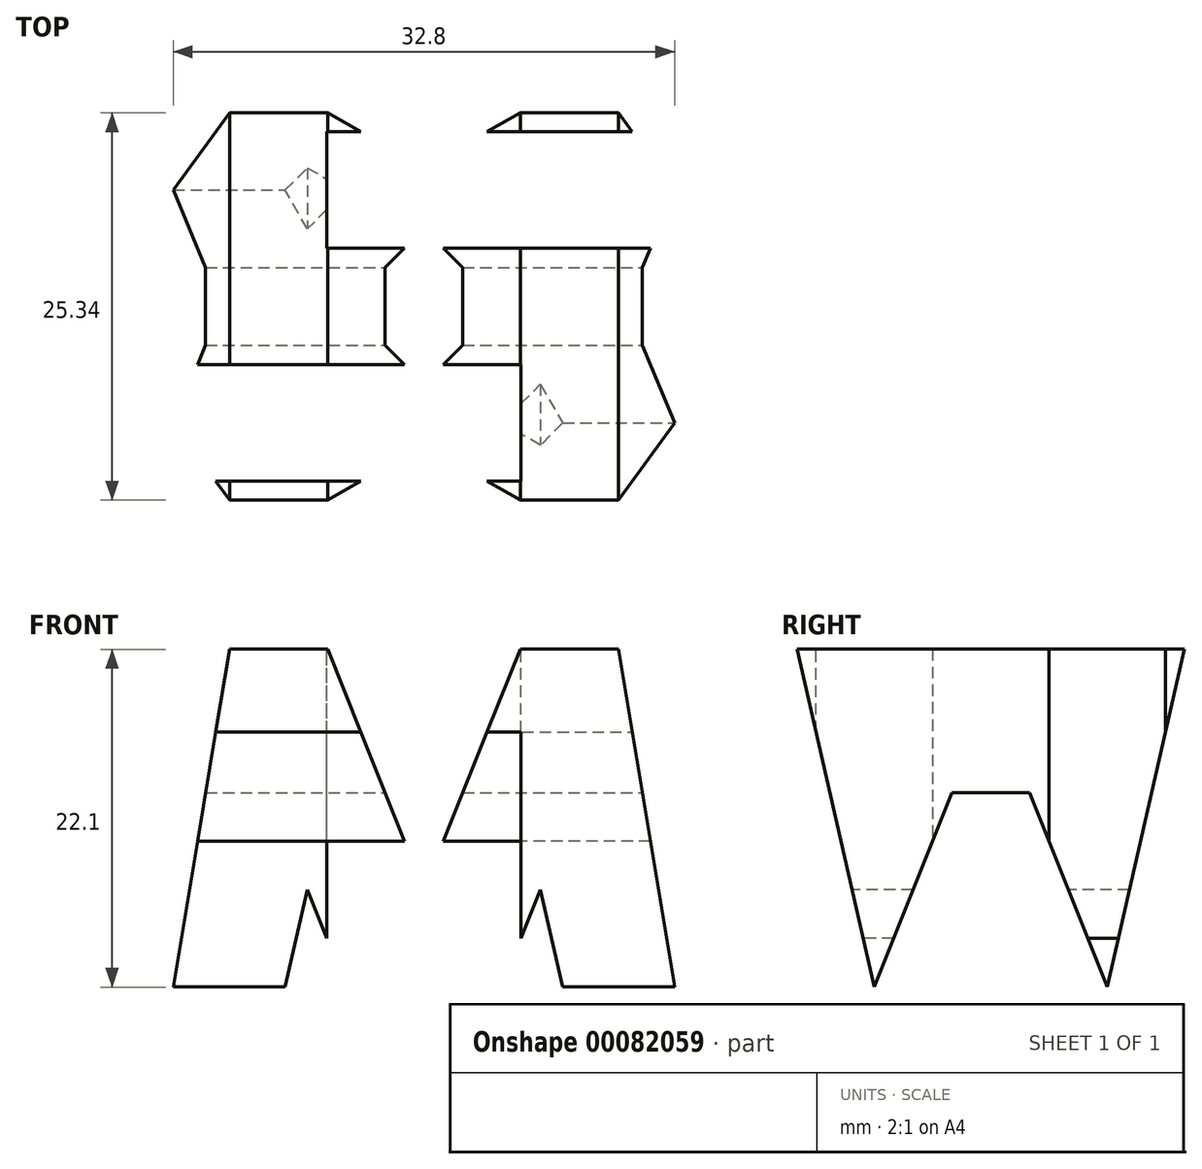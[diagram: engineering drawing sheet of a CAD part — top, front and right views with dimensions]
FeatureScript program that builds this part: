
annotation { "Feature Type Name" : "Feature", "Feature Type Description" : "" }
export const myFeature = defineFeature(function(context is Context, id is Id, definition is map)
    precondition{}
    {
        {
            var Q0;
            Q0=qCreatedBy(makeId("Front.planeOp"),FACE);
            var sketch = newSketch(context, id + "F0", { "sketchPlane" : qUnion([Q0])});
            skLineSegment(sketch, "E0", {"start": v(0, 0) * mm, "end": v(0, 37.97) * mm});
            skLineSegment(sketch, "E1", {"start": v(0, 37.97) * mm, "end": v(38.1, 37.97) * mm});
            skLineSegment(sketch, "E2", {"start": v(38.1, 37.97) * mm, "end": v(38.1, 0) * mm});
            skLineSegment(sketch, "E3", {"start": v(38.1, 0) * mm, "end": v(0, 0) * mm});
            skSolve(sketch);
        }
        {
            var Q0;
            Q0 = qSketchRegion(id + "F0", true);
            extrude(context, id + "F1", {"entities" : qUnion([Q0]), "depth" : 38.1 * mm});
        }
        {
            var Q0;
            Q0=qCreatedBy(makeId("Front.planeOp"),FACE);
            cPlane(context, id + "F2", {"entities" : qUnion([Q0]), "cplaneType" : CPlaneType.OFFSET, "offset" : 38.1 * mm, "width" : 152.4 * mm, "height" : 152.4 * mm});
        }
        {
            var Q0;
            Q0=qCreatedBy(makeId("Right.planeOp"),FACE);
            cPlane(context, id + "F3", {"entities" : qUnion([Q0]), "cplaneType" : CPlaneType.OFFSET, "offset" : 38.1 * mm, "width" : 152.4 * mm, "height" : 152.4 * mm});
        }
        {
            var Q0;
            Q0=qCreatedBy(makeId("Top.planeOp"),FACE);
            cPlane(context, id + "F4", {"entities" : qUnion([Q0]), "cplaneType" : CPlaneType.OFFSET, "offset" : 38.1 * mm, "width" : 152.4 * mm, "height" : 152.4 * mm});
        }
        {
            var Q0;
            Q0=qCreatedBy(id+"F3.planeOp",FACE);
            var sketch = newSketch(context, id + "F5", { "sketchPlane" : qUnion([Q0])});
            skLineSegment(sketch, "E4", {"start": v(0, 0) * mm, "end": v(0, 38.1) * mm});
            skLineSegment(sketch, "E5", {"start": v(0, 38.1) * mm, "end": v(-38.1, 38.1) * mm});
            skLineSegment(sketch, "E6", {"start": v(-38.1, 38.1) * mm, "end": v(-38.1, 0) * mm});
            skLineSegment(sketch, "E7", {"start": v(-38.1, 0) * mm, "end": v(0, 0) * mm});
            skLineSegment(sketch, "E8", {"start": v(-38.1, 38.1) * mm, "end": v(-31.75, 0) * mm});
            skLineSegment(sketch, "E9", {"start": v(-31.75, 0) * mm, "end": v(-25.4, 0) * mm});
            skLineSegment(sketch, "E10", {"start": v(-12.7, 0) * mm, "end": v(-6.35, 0) * mm});
            skLineSegment(sketch, "E11", {"start": v(-6.35, 0) * mm, "end": v(0, 38.1) * mm});
            skLineSegment(sketch, "E12", {"start": v(-38.1, 38.1) * mm, "end": v(-31.75, 38.1) * mm});
            skLineSegment(sketch, "E13", {"start": v(-6.35, 38.1) * mm, "end": v(0, 38.1) * mm});
            skLineSegment(sketch, "E14", {"start": v(-25.4, 0) * mm, "end": v(-19.05, 15.88) * mm});
            skLineSegment(sketch, "E15", {"start": v(-19.05, 15.88) * mm, "end": v(-12.7, 0) * mm});
            skLineSegment(sketch, "E16", {"start": v(-31.75, 38.1) * mm, "end": v(-26.67, 15.88) * mm});
            skLineSegment(sketch, "E17", {"start": v(-26.67, 15.88) * mm, "end": v(-21.59, 28.58) * mm});
            skLineSegment(sketch, "E18", {"start": v(-16.5, 28.58) * mm, "end": v(-11.43, 15.88) * mm});
            skLineSegment(sketch, "E19", {"start": v(-11.43, 15.88) * mm, "end": v(-6.35, 38.1) * mm});
            skPoint(sketch, "E20.orphan", {"position": v(-27.94, 38.1) * mm});
            skPoint(sketch, "E21.trimOffspring.end.orphan", {"position": v(-20.93, 0) * mm});
            skPoint(sketch, "E22.orphan", {"position": v(-10.16, 38.1) * mm});
            skLineSegment(sketch, "E23", {"start": v(-21.59, 28.58) * mm, "end": v(-16.5, 28.58) * mm});
            skSolve(sketch);
        }
        {
            var Q0;
            Q0=makeQuery(id+"F5.imprint","IMPRINT",FACE,{"disambiguationData":[TD([[makeQuery(id+"F5.imprint","IMPRINT",EDGE,{"derivedFrom":sQuery(id+"F5.wireOp",EDGE,"E5")}),1.0]])]});
            var Q1;
            {var subQ0=sQuery(id+"F5.wireOp",EDGE,"E4");Q1=makeQuery(id+"F5.imprint","IMPRINT",FACE,{"disambiguationData":[TD([[makeQuery(id+"F5.imprint","IMPRINT",EDGE,{"derivedFrom":subQ0}),1.0]])]});}
            var Q2;
            {var subQ0=sQuery(id+"F5.wireOp",EDGE,"E14");Q2=makeQuery(id+"F5.imprint","IMPRINT",FACE,{"disambiguationData":[TD([[makeQuery(id+"F5.imprint","IMPRINT",EDGE,{"derivedFrom":subQ0}),-1.0]])]});}
            var Q3;
            {var subQ0=sQuery(id+"F5.wireOp",EDGE,"E6");Q3=makeQuery(id+"F5.imprint","IMPRINT",FACE,{"disambiguationData":[TD([[makeQuery(id+"F5.imprint","IMPRINT",EDGE,{"derivedFrom":subQ0}),1.0]])]});}
            extrude(context, id + "F6", {"entities" : qUnion([Q0, Q1, Q2, Q3]), "operationType" : NewBodyOperationType.REMOVE, "oppositeDirection" : true, "depth" : 38.1 * mm});
        }
        {
            var Q0;
            Q0=qCreatedBy(id+"F2.planeOp",FACE);
            var sketch = newSketch(context, id + "F7", { "sketchPlane" : qUnion([Q0])});
            skLineSegment(sketch, "E24", {"start": v(0, 0) * mm, "end": v(6.35, 38.1) * mm});
            skLineSegment(sketch, "E25", {"start": v(6.35, 38.1) * mm, "end": v(12.7, 38.1) * mm});
            skLineSegment(sketch, "E26", {"start": v(25.4, 38.1) * mm, "end": v(31.75, 38.1) * mm});
            skLineSegment(sketch, "E27", {"start": v(31.75, 38.1) * mm, "end": v(38.1, 0) * mm});
            skLineSegment(sketch, "E28", {"start": v(38.1, 0) * mm, "end": v(31.75, 0) * mm});
            skLineSegment(sketch, "E29", {"start": v(31.75, 0) * mm, "end": v(26.67, 22.23) * mm});
            skLineSegment(sketch, "E30", {"start": v(26.67, 22.23) * mm, "end": v(21.59, 9.52) * mm});
            skLineSegment(sketch, "E31", {"start": v(21.59, 9.53) * mm, "end": v(16.51, 9.53) * mm});
            skLineSegment(sketch, "E32", {"start": v(16.51, 9.53) * mm, "end": v(11.43, 22.23) * mm});
            skLineSegment(sketch, "E33", {"start": v(11.43, 22.23) * mm, "end": v(6.35, 0) * mm});
            skLineSegment(sketch, "E34", {"start": v(6.35, 0) * mm, "end": v(0, 0) * mm});
            skLineSegment(sketch, "E35", {"start": v(12.7, 38.1) * mm, "end": v(19.05, 22.22) * mm});
            skLineSegment(sketch, "E36", {"start": v(19.05, 22.22) * mm, "end": v(25.4, 38.1) * mm});
            skLineSegment(sketch, "E37.bottom", {"start": v(0, 0) * mm, "end": v(38.1, 0) * mm});
            skLineSegment(sketch, "E37.top", {"start": v(0, 38.1) * mm, "end": v(38.1, 38.1) * mm});
            skLineSegment(sketch, "E37.left", {"start": v(0, 0) * mm, "end": v(0, 38.1) * mm});
            skLineSegment(sketch, "E37.right", {"start": v(38.1, 0) * mm, "end": v(38.1, 38.1) * mm});
            skSolve(sketch);
        }
        {
            var Q0;
            {var subQ0=sQuery(id+"F7.wireOp",EDGE,"E29");Q0=makeQuery(id+"F7.imprint","IMPRINT",FACE,{"disambiguationData":[TD([[makeQuery(id+"F7.imprint","IMPRINT",EDGE,{"derivedFrom":subQ0}),1.0]])]});}
            var Q1;
            {var subQ0=sQuery(id+"F7.wireOp",EDGE,"E35");Q1=makeQuery(id+"F7.imprint","IMPRINT",FACE,{"disambiguationData":[TD([[makeQuery(id+"F7.imprint","IMPRINT",EDGE,{"derivedFrom":subQ0}),1.0]])]});}
            var Q2;
            {var subQ0=sQuery(id+"F7.wireOp",EDGE,"E27");Q2=makeQuery(id+"F7.imprint","IMPRINT",FACE,{"disambiguationData":[TD([[makeQuery(id+"F7.imprint","IMPRINT",EDGE,{"derivedFrom":subQ0}),1.0]])]});}
            var Q3;
            {var subQ0=sQuery(id+"F7.wireOp",EDGE,"E24");Q3=makeQuery(id+"F7.imprint","IMPRINT",FACE,{"disambiguationData":[TD([[makeQuery(id+"F7.imprint","IMPRINT",EDGE,{"derivedFrom":subQ0}),1.0]])]});}
            extrude(context, id + "F8", {"entities" : qUnion([Q0, Q1, Q2, Q3]), "operationType" : NewBodyOperationType.REMOVE, "oppositeDirection" : true, "depth" : 38.1 * mm});
        }
        {
            var Q0;
            Q0=qCreatedBy(id+"F4.planeOp",FACE);
            var sketch = newSketch(context, id + "F9", { "sketchPlane" : qUnion([Q0])});
            skLineSegment(sketch, "E38", {"start": v(0, 0) * mm, "end": v(0, -38.1) * mm});
            skLineSegment(sketch, "E39", {"start": v(0, -38.1) * mm, "end": v(38.1, -38.1) * mm});
            skLineSegment(sketch, "E40", {"start": v(38.1, -38.1) * mm, "end": v(38.1, 0) * mm});
            skLineSegment(sketch, "E41", {"start": v(38.1, 0) * mm, "end": v(0, 0) * mm});
            skLineSegment(sketch, "E42", {"start": v(38.1, -7.62) * mm, "end": v(12.7, -7.62) * mm});
            skLineSegment(sketch, "E43", {"start": v(12.7, -7.62) * mm, "end": v(12.7, -15.24) * mm});
            skLineSegment(sketch, "E44", {"start": v(12.7, -15.24) * mm, "end": v(38.1, -15.24) * mm});
            skLineSegment(sketch, "E45", {"start": v(38.1, -15.24) * mm, "end": v(38.1, -7.62) * mm});
            skLineSegment(sketch, "E46", {"start": v(0, -22.86) * mm, "end": v(25.4, -22.86) * mm});
            skLineSegment(sketch, "E47", {"start": v(25.4, -22.86) * mm, "end": v(25.4, -30.48) * mm});
            skLineSegment(sketch, "E48", {"start": v(25.4, -30.48) * mm, "end": v(0, -30.48) * mm});
            skLineSegment(sketch, "E49", {"start": v(0, -30.48) * mm, "end": v(0, -22.86) * mm});
            skSolve(sketch);
        }
        {
            var Q0;
            Q0=makeQuery(id+"F9.imprint","IMPRINT",FACE,{"disambiguationData":[TD([[makeQuery(id+"F9.imprint","IMPRINT",EDGE,{"derivedFrom":sQuery(id+"F9.wireOp",EDGE,"E42")}),1.0]])]});
            var Q1;
            Q1=makeQuery(id+"F9.imprint","IMPRINT",FACE,{"disambiguationData":[TD([[makeQuery(id+"F9.imprint","IMPRINT",EDGE,{"derivedFrom":sQuery(id+"F9.wireOp",EDGE,"E46")}),-1.0]])]});
            extrude(context, id + "F10", {"entities" : qUnion([Q0, Q1]), "operationType" : NewBodyOperationType.REMOVE, "oppositeDirection" : true, "depth" : 38.1 * mm});
        }
    });
